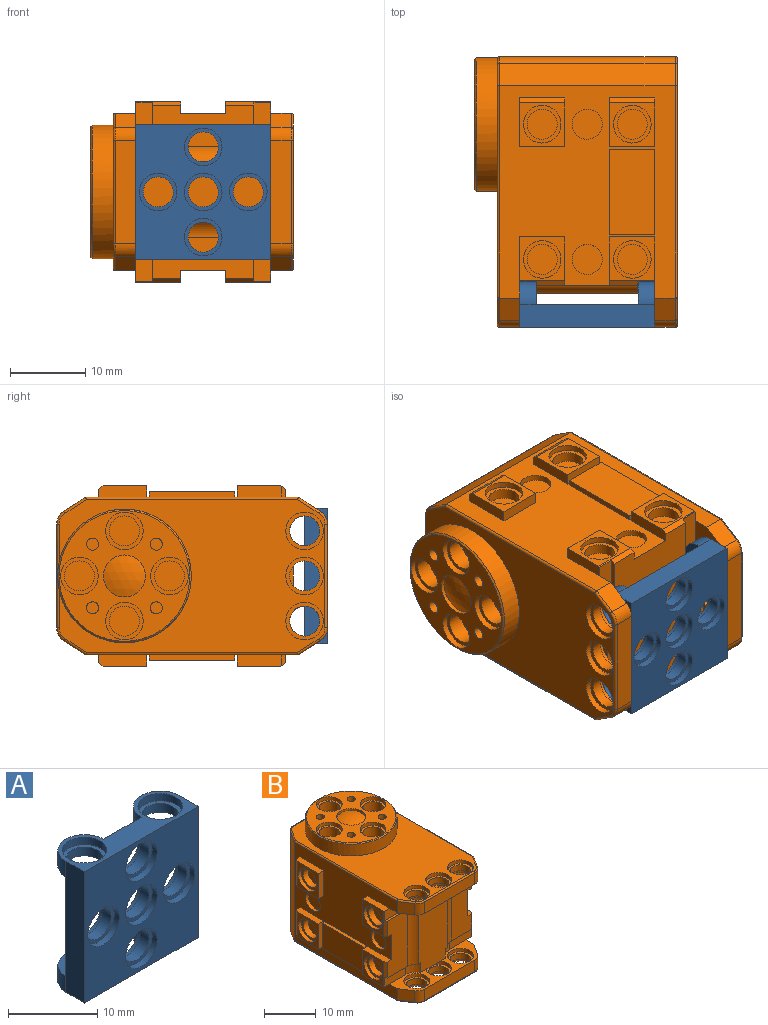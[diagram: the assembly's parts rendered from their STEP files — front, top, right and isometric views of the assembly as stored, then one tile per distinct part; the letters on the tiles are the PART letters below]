
ASSEMBLY  parts=2 mates=1
PART A: 59 faces, bbox 18x6x18 mm
  f0: plane 18x6mm, normal (0,0,-1), area 43mm2, adj f50,f51,f52,f53,f54,f55,f56,f58
  f1: plane 5x5mm, normal (0,0,1), area 7.1mm2, adj f13,f15
  f2: plane 5x5mm, normal (0,0,1), area 7.1mm2, adj f14,f16
  f3: cylinder r=2mm len=4mm, axis (0,1,0), area 17.6mm2, adj f8,f17
  f4: cylinder r=2mm len=4mm, axis (0,1,0), area 17.6mm2, adj f9,f18
  f5: cylinder r=2mm len=4mm, axis (0,1,0), area 17.6mm2, adj f10,f19
  f6: cylinder r=2mm len=4mm, axis (0,1,0), area 17.6mm2, adj f11,f20
  f7: cylinder r=2mm len=4mm, axis (0,1,0), area 17.6mm2, adj f12,f21
  f8: plane 5x5mm, normal (0,-1,0), area 7.1mm2, adj f3,f23
  f9: plane 5x5mm, normal (0,-1,0), area 7.1mm2, adj f4,f24
  f10: plane 5x5mm, normal (0,-1,0), area 7.1mm2, adj f5,f25
  f11: plane 5x5mm, normal (0,-1,0), area 7.1mm2, adj f6,f26
  f12: plane 5x5mm, normal (0,-1,0), area 7.1mm2, adj f7,f27
  f13: cylinder r=2mm len=4mm, axis (0,0,-1), area 15.1mm2, adj f1,f31
  f14: cylinder r=2mm len=4mm, axis (0,0,-1), area 15.1mm2, adj f2,f40
  f15: cylinder r=2.5mm len=5mm, axis (0,0,-1), area 15.7mm2, adj f1,f42
  f16: cylinder r=2.5mm len=5mm, axis (0,0,-1), area 15.7mm2, adj f2,f42
  f17: plane 5x5mm, normal (0,1,0), area 7.1mm2, adj f3,f43
  f18: plane 5x5mm, normal (0,1,0), area 7.1mm2, adj f4,f44
  f19: plane 5x5mm, normal (0,1,0), area 7.1mm2, adj f5,f45
  f20: plane 5x5mm, normal (0,1,0), area 7.1mm2, adj f6,f46
  f21: plane 5x5mm, normal (0,1,0), area 7.1mm2, adj f7,f47
  f22: cylinder r=2mm len=4mm, axis (0,0,1), area 15.1mm2, adj f34,f48
  f23: cylinder r=2.5mm len=5mm, axis (0,1,0), area 12.6mm2, adj f8,f52
  f24: cylinder r=2.5mm len=5mm, axis (0,1,0), area 12.6mm2, adj f9,f52
  f25: cylinder r=2.5mm len=5mm, axis (0,1,0), area 12.6mm2, adj f10,f52
  f26: cylinder r=2.5mm len=5mm, axis (0,1,0), area 12.6mm2, adj f11,f52
  f27: cylinder r=2.5mm len=5mm, axis (0,1,0), area 12.6mm2, adj f12,f52
  f28: cylinder r=3mm len=6mm, axis (0,0,-1), area 20.7mm2, adj f31,f42,f51,f55
  f29: plane 5x2.5mm, normal (0,0,1), area 9.8mm2, adj f30,f55
  f30: cylinder r=2.5mm len=5mm, axis (0,0,-1), area 6.3mm2, adj f29,f31,f55
  f31: plane 6x5.5mm, normal (0,0,-1), area 11.4mm2, adj f13,f28,f30,f55
  f32: plane 5x2.5mm, normal (0,0,-1), area 9.8mm2, adj f33,f55
  f33: cylinder r=2.5mm len=5mm, axis (0,0,1), area 6.3mm2, adj f32,f34,f55
  f34: plane 6x5.5mm, normal (0,0,1), area 11.4mm2, adj f22,f33,f50,f55
  f35: plane 5x2.5mm, normal (0,0,-1), area 9.8mm2, adj f36,f55
  f36: cylinder r=2.5mm len=5mm, axis (0,0,1), area 6.3mm2, adj f35,f37,f55
  f37: plane 6x5.5mm, normal (0,0,1), area 11.4mm2, adj f36,f49,f54,f55
  f38: plane 5x2.5mm, normal (0,0,1), area 9.8mm2, adj f39,f55
  f39: cylinder r=2.5mm len=5mm, axis (0,0,-1), area 6.3mm2, adj f38,f40,f55
  f40: plane 6x5.5mm, normal (0,0,-1), area 11.4mm2, adj f14,f39,f41,f55
  f41: cylinder r=3mm len=6mm, axis (0,0,-1), area 20.7mm2, adj f40,f42,f53,f55
  f42: plane 18x6mm, normal (0,0,1), area 43mm2, adj f15,f16,f28,f41,f51,f52,f53,f55
  f43: cylinder r=2.5mm len=5mm, axis (0,-1,0), area 12.6mm2, adj f17,f55
  f44: cylinder r=2.5mm len=5mm, axis (0,-1,0), area 12.6mm2, adj f18,f55
  f45: cylinder r=2.5mm len=5mm, axis (0,-1,0), area 12.6mm2, adj f19,f55
  f46: cylinder r=2.5mm len=5mm, axis (0,-1,0), area 12.6mm2, adj f20,f55
  f47: cylinder r=2.5mm len=5mm, axis (0,-1,0), area 12.6mm2, adj f21,f55
  f48: plane 5x5mm, normal (0,0,-1), area 7.1mm2, adj f22,f56
  f49: cylinder r=2mm len=4mm, axis (0,0,1), area 15.1mm2, adj f37,f57
  f50: cylinder r=3mm len=6mm, axis (0,0,1), area 20.7mm2, adj f0,f34,f51,f55
  f51: plane 18x3mm, normal (-1,0,0), area 54mm2, adj f0,f28,f42,f50,f52,f55
  f52: plane 18x18mm, normal (0,-1,0), area 225.8mm2, adj f0,f23,f24,f25,f26,f27,f42,f51
  f53: plane 18x3mm, normal (1,0,0), area 54mm2, adj f0,f41,f42,f52,f54,f55
  f54: cylinder r=3mm len=6mm, axis (0,0,1), area 20.7mm2, adj f0,f37,f53,f55
  f55: plane 18x18mm, normal (0,1,0), area 157mm2, adj f0,f28,f29,f30,f31,f32,f33,f34
  f56: cylinder r=2.5mm len=5mm, axis (0,0,1), area 15.7mm2, adj f0,f48
  f57: plane 5x5mm, normal (0,0,-1), area 7.1mm2, adj f49,f58
  f58: cylinder r=2.5mm len=5mm, axis (0,0,1), area 15.7mm2, adj f0,f57
PART B: 229 faces, bbox 24x36.3x27 mm
  f0: torus R=1.7mm, axis (0,0,1), area 0.9mm2, adj f2,f5,f98,f144
  f1: torus R=1.7mm, axis (0,0,1), area 0.9mm2, adj f4,f6,f98,f144
  f2: cylinder r=0.3mm len=3.1mm, axis (-0.54,0.84,0), area 1.6mm2, adj f0,f11,f144,f150
  f3: cylinder r=2.5mm len=13.5mm, axis (0,0,-1), area 31.3mm2, adj f103,f104,f129,f154
  f4: cylinder r=0.3mm len=3.1mm, axis (-0.54,-0.84,0), area 1.6mm2, adj f1,f14,f144,f170
  f5: cylinder r=2mm len=2.7mm, axis (0,0,-1), area 5.4mm2, adj f0,f132,f150,f179
  f6: cylinder r=2mm len=2.7mm, axis (0,0,-1), area 5.4mm2, adj f1,f132,f170,f179
  f7: cylinder r=0.3mm len=3.1mm, axis (0.54,-0.84,0), area 1.6mm2, adj f8,f14,f144,f207
  f8: torus R=1.7mm, axis (0,0,-1), area 0.9mm2, adj f7,f144,f191,f208
  f9: cylinder r=8.9mm len=17.8mm, axis (0,0,-1), area 156.6mm2, adj f97,f144,f191
  f10: cylinder r=2.5mm len=5mm, axis (0,0,-1), area 12.6mm2, adj f171,f199
  f11: cylinder r=0.3mm len=28.3mm, axis (0,1,0), area 13.3mm2, adj f2,f144,f193,f200
  f12: cylinder r=2mm len=4mm, axis (-1,0,0), area 10.1mm2, adj f109,f200
  f13: cylinder r=2mm len=4mm, axis (-1,0,0), area 10.1mm2, adj f110,f200
  f14: cylinder r=0.3mm len=28.3mm, axis (0,-1,0), area 13.3mm2, adj f4,f7,f144,f206
  f15: cylinder r=2mm len=4mm, axis (-1,0,0), area 10.1mm2, adj f138,f206
  f16: cylinder r=2mm len=4mm, axis (-1,0,0), area 10.1mm2, adj f139,f206
  f17: plane 11.4x0.7mm, normal (0,0,-1), area 8mm2, adj f137,f180,f182,f206
  f18: cylinder r=2.5mm len=5mm, axis (0,0,1), area 12.6mm2, adj f19,f20
  f19: plane 35.4x20.4mm, normal (0,0,-1), area 586.6mm2, adj f18,f21,f22,f23,f24,f25,f26,f218
  f20: plane 5x5mm, normal (0,0,-1), area 7.1mm2, adj f18,f217
  f21: cylinder r=2.5mm len=5mm, axis (0,0,1), area 12.6mm2, adj f19,f216
  f22: torus R=1.7mm, axis (0,0,1), area 0.9mm2, adj f19,f202,f219,f220
  f23: torus R=1.7mm, axis (0,0,1), area 0.9mm2, adj f19,f204,f220,f221
  f24: cylinder r=0.3mm len=3.1mm, axis (-0.54,0.84,0), area 1.6mm2, adj f19,f25,f207,f222
  f25: torus R=1.7mm, axis (0,0,-1), area 0.9mm2, adj f19,f24,f208,f223
  f26: torus R=1.7mm, axis (0,0,-1), area 0.9mm2, adj f19,f210,f223,f224
  f27: plane 4x4mm, normal (0,0,1), area 12.6mm2, adj f31
  f28: plane 4x4mm, normal (0,0,1), area 12.6mm2, adj f32
  f29: plane 4x4mm, normal (0,0,1), area 12.6mm2, adj f33
  f30: plane 4x4mm, normal (0,0,1), area 12.6mm2, adj f34
  f31: cylinder r=2mm len=4mm, axis (0,0,-1), area 27.6mm2, adj f27,f48
  f32: cylinder r=2mm len=4mm, axis (0,0,-1), area 27.6mm2, adj f28,f49
  f33: cylinder r=2mm len=4mm, axis (0,0,-1), area 27.6mm2, adj f29,f50
  f34: cylinder r=2mm len=4mm, axis (0,0,-1), area 27.6mm2, adj f30,f51
  f35: plane 4x4mm, normal (-1,0,0), area 12.6mm2, adj f52
  f36: plane 4x4mm, normal (-1,0,0), area 12.6mm2, adj f53
  f37: plane 4x4mm, normal (-1,0,0), area 12.6mm2, adj f54
  f38: plane 4x4mm, normal (-1,0,0), area 12.6mm2, adj f55
  f39: plane 4x4mm, normal (1,0,0), area 12.6mm2, adj f56
  f40: plane 4x4mm, normal (1,0,0), area 12.6mm2, adj f57
  f41: plane 4x4mm, normal (1,0,0), area 12.6mm2, adj f58
  f42: plane 4x4mm, normal (1,0,0), area 12.6mm2, adj f59
  f43: plane 1.6x1.6mm, normal (0,0,1), area 2mm2, adj f60
  f44: plane 1.6x1.6mm, normal (0,0,1), area 2mm2, adj f61
  f45: plane 1.6x1.6mm, normal (0,0,1), area 2mm2, adj f62
  f46: plane 1.6x1.6mm, normal (0,0,1), area 2mm2, adj f63
  f47: sphere r=8.09mm, area 25.4mm2, adj f64
  f48: plane 5x5mm, normal (0,0,1), area 7.1mm2, adj f31,f65
  f49: plane 5x5mm, normal (0,0,1), area 7.1mm2, adj f32,f66
  f50: plane 5x5mm, normal (0,0,1), area 7.1mm2, adj f33,f67
  f51: plane 5x5mm, normal (0,0,1), area 7.1mm2, adj f34,f68
  f52: cylinder r=2mm len=4mm, axis (-1,0,0), area 17.6mm2, adj f35,f69
  f53: cylinder r=2mm len=4mm, axis (-1,0,0), area 17.6mm2, adj f36,f70
  f54: cylinder r=2mm len=4mm, axis (-1,0,0), area 17.6mm2, adj f37,f71
  f55: cylinder r=2mm len=4mm, axis (-1,0,0), area 17.6mm2, adj f38,f72
  f56: cylinder r=2mm len=4mm, axis (-1,0,0), area 17.6mm2, adj f39,f73
  f57: cylinder r=2mm len=4mm, axis (-1,0,0), area 17.6mm2, adj f40,f74
  f58: cylinder r=2mm len=4mm, axis (-1,0,0), area 17.6mm2, adj f41,f78
  f59: cylinder r=2mm len=4mm, axis (-1,0,0), area 17.6mm2, adj f42,f79
  f60: cylinder r=0.8mm len=3mm, axis (0,0,-1), area 15.1mm2, adj f43,f80
  f61: cylinder r=0.8mm len=3mm, axis (0,0,-1), area 15.1mm2, adj f44,f80
  f62: cylinder r=0.8mm len=3mm, axis (0,0,-1), area 15.1mm2, adj f45,f80
  f63: cylinder r=0.8mm len=3mm, axis (0,0,-1), area 15.1mm2, adj f46,f80
  f64: cylinder r=2.8mm len=5.6mm, axis (0,0,-1), area 8.8mm2, adj f47,f80
  f65: cylinder r=2.5mm len=5mm, axis (0,0,-1), area 12.6mm2, adj f48,f80
  f66: cylinder r=2.5mm len=5mm, axis (0,0,-1), area 12.6mm2, adj f49,f80
  f67: cylinder r=2.5mm len=5mm, axis (0,0,-1), area 12.6mm2, adj f50,f80
  f68: cylinder r=2.5mm len=5mm, axis (0,0,-1), area 12.6mm2, adj f51,f80
  f69: plane 5x5mm, normal (-1,0,0), area 7.1mm2, adj f52,f84
  f70: plane 5x5mm, normal (-1,0,0), area 7.1mm2, adj f53,f85
  f71: plane 5x5mm, normal (-1,0,0), area 7.1mm2, adj f54,f86
  f72: plane 5x5mm, normal (-1,0,0), area 7.1mm2, adj f55,f87
  f73: plane 5x5mm, normal (1,0,0), area 7.1mm2, adj f56,f88
  f74: plane 5x5mm, normal (1,0,0), area 7.1mm2, adj f57,f89
  f75: cylinder r=2mm len=4mm, axis (0,0,-1), area 17.6mm2, adj f82,f90
  f76: cylinder r=2mm len=4mm, axis (0,0,-1), area 17.6mm2, adj f81,f93
  f77: cylinder r=2mm len=4mm, axis (0,0,-1), area 17.6mm2, adj f83,f94
  f78: plane 5x5mm, normal (1,0,0), area 7.1mm2, adj f58,f95
  f79: plane 5x5mm, normal (1,0,0), area 7.1mm2, adj f59,f96
  f80: plane 17.4x17.4mm, normal (0,0,1), area 126.6mm2, adj f60,f61,f62,f63,f64,f65,f66,f67
  f81: plane 5x5mm, normal (0,0,1), area 7.1mm2, adj f76,f99
  f82: plane 5x5mm, normal (0,0,1), area 7.1mm2, adj f75,f100
  f83: plane 5x5mm, normal (0,0,1), area 7.1mm2, adj f77,f101
  f84: cylinder r=2.5mm len=5mm, axis (-1,0,0), area 12.6mm2, adj f69,f102
  f85: cylinder r=2.5mm len=5mm, axis (-1,0,0), area 12.6mm2, adj f70,f107
  f86: cylinder r=2.5mm len=5mm, axis (-1,0,0), area 12.6mm2, adj f71,f112
  f87: cylinder r=2.5mm len=5mm, axis (-1,0,0), area 12.6mm2, adj f72,f114
  f88: cylinder r=2.5mm len=5mm, axis (-1,0,0), area 12.6mm2, adj f73,f121
  f89: cylinder r=2.5mm len=5mm, axis (-1,0,0), area 12.6mm2, adj f74,f127
  f90: plane 5x5mm, normal (0,0,-1), area 7.1mm2, adj f75,f128
  f91: plane 4x1mm, normal (0,0,-1), area 2.8mm2, adj f115,f129
  f92: plane 4x1mm, normal (0,0,1), area 2.8mm2, adj f128,f129
  f93: plane 5x5mm, normal (0,0,-1), area 7.1mm2, adj f76,f135
  f94: plane 5x5mm, normal (0,0,-1), area 7.1mm2, adj f77,f136
  f95: cylinder r=2.5mm len=5mm, axis (-1,0,0), area 12.6mm2, adj f78,f141
  f96: cylinder r=2.5mm len=5mm, axis (-1,0,0), area 12.6mm2, adj f79,f143
  f97: cone r=707.11mm half-angle=45deg, axis (0,0,-1), area 15.6mm2, adj f9,f80
  f98: cylinder r=0.3mm len=13.83mm, axis (-1,0,0), area 6.5mm2, adj f0,f1,f132,f144
  f99: cylinder r=2.5mm len=5mm, axis (0,0,-1), area 12.6mm2, adj f81,f144
  f100: cylinder r=2.5mm len=5mm, axis (0,0,-1), area 12.6mm2, adj f82,f144
  f101: cylinder r=2.5mm len=5mm, axis (0,0,-1), area 12.6mm2, adj f83,f144
  f102: plane 6x5.84mm, normal (-1,0,0), area 15.4mm2, adj f84,f105,f151,f152,f153
  f103: plane 8.54x1.53mm, normal (0,0,-1), area 4.5mm2, adj f3,f106,f116,f117,f129,f154
  f104: plane 8.54x1.53mm, normal (0,0,1), area 4.5mm2, adj f3,f105,f129,f130,f131,f154
  f105: plane 6x0.66mm, normal (-0.84,-0.54,0), area 3.3mm2, adj f102,f104,f131,f151,f153,f154
  f106: plane 6x0.66mm, normal (-0.84,-0.54,0), area 3.3mm2, adj f103,f107,f117,f154,f155,f157
  f107: plane 6x5.84mm, normal (-1,0,0), area 15.4mm2, adj f85,f106,f155,f156,f157
  f108: plane 11.4x6mm, normal (-1,0,0), area 68.4mm2, adj f158,f159,f160,f161
  f109: plane 4x4mm, normal (-1,0,0), area 12.6mm2, adj f12
  f110: plane 4x4mm, normal (-1,0,0), area 12.6mm2, adj f13
  f111: plane 6x0.66mm, normal (-0.84,0.54,0), area 4.7mm2, adj f112,f163,f164,f165
  f112: plane 6x5.84mm, normal (-1,0,0), area 15.4mm2, adj f86,f111,f162,f163,f165
  f113: plane 6x0.66mm, normal (-0.84,0.54,0), area 4.7mm2, adj f114,f167,f168,f169
  f114: plane 6x5.84mm, normal (-1,0,0), area 15.4mm2, adj f87,f113,f166,f167,f169
  f115: cylinder r=2.5mm len=5mm, axis (0,0,-1), area 12.6mm2, adj f91,f145,f171
  f116: cylinder r=3.02mm len=2.63mm, axis (0,0,-1), area 7.2mm2, adj f103,f117,f129,f171
  f117: plane 5.91x2.25mm, normal (0,-1,0), area 13.3mm2, adj f103,f106,f116,f157,f171
  f118: cylinder r=3.02mm len=2.63mm, axis (0,0,-1), area 7.2mm2, adj f120,f124,f129,f171
  f119: cylinder r=2.5mm len=5mm, axis (0,0,-1), area 12.6mm2, adj f146,f171
  f120: plane 5.91x2.25mm, normal (0,-1,0), area 13.3mm2, adj f118,f124,f125,f171,f172
  f121: plane 6x5.84mm, normal (1,0,0), area 15.4mm2, adj f88,f125,f172,f173,f174
  f122: plane 8.54x1.53mm, normal (0,0,1), area 4.5mm2, adj f123,f126,f129,f133,f134,f175
  f123: cylinder r=2.5mm len=13.5mm, axis (0,0,-1), area 31.3mm2, adj f122,f124,f129,f175
  f124: plane 8.54x1.53mm, normal (0,0,-1), area 4.5mm2, adj f118,f120,f123,f125,f129,f175
  f125: plane 6x0.66mm, normal (0.84,-0.54,0), area 3.3mm2, adj f120,f121,f124,f172,f174,f175
  f126: plane 6x0.66mm, normal (0.84,-0.54,0), area 3.3mm2, adj f122,f127,f133,f175,f176,f178
  f127: plane 6x5.84mm, normal (1,0,0), area 15.4mm2, adj f89,f126,f176,f177,f178
  f128: cylinder r=2.5mm len=5mm, axis (0,0,-1), area 12.6mm2, adj f90,f92,f179
  f129: plane 18x8mm, normal (0,-1,0), area 138.4mm2, adj f3,f91,f92,f103,f104,f116,f118,f122
  f130: cylinder r=3.02mm len=2.63mm, axis (0,0,-1), area 7.2mm2, adj f104,f129,f131,f179
  f131: plane 5.91x2.25mm, normal (0,-1,0), area 13.3mm2, adj f104,f105,f130,f151,f179
  f132: plane 13.83x2.7mm, normal (0,-1,0), area 37.3mm2, adj f5,f6,f98,f179
  f133: plane 5.91x2.25mm, normal (0,-1,0), area 13.3mm2, adj f122,f126,f134,f178,f179
  f134: cylinder r=3.02mm len=2.63mm, axis (0,0,-1), area 7.2mm2, adj f122,f129,f133,f179
  f135: cylinder r=2.5mm len=5mm, axis (0,0,-1), area 12.6mm2, adj f93,f179
  f136: cylinder r=2.5mm len=5mm, axis (0,0,-1), area 12.6mm2, adj f94,f179
  f137: plane 11.4x6mm, normal (1,0,0), area 68.4mm2, adj f17,f180,f181,f182
  f138: plane 4x4mm, normal (1,0,0), area 12.6mm2, adj f15
  f139: plane 4x4mm, normal (1,0,0), area 12.6mm2, adj f16
  f140: plane 6x0.66mm, normal (0.84,0.54,0), area 4.7mm2, adj f141,f184,f185,f186
  f141: plane 6x5.84mm, normal (1,0,0), area 15.4mm2, adj f95,f140,f183,f184,f186
  f142: plane 6x0.66mm, normal (0.84,0.54,0), area 4.7mm2, adj f143,f188,f189,f190
  f143: plane 6x5.84mm, normal (1,0,0), area 15.4mm2, adj f96,f142,f187,f188,f190
  f144: plane 35.4x20.4mm, normal (0,0,1), area 397.2mm2, adj f0,f1,f2,f4,f7,f8,f9,f11
  f145: plane 5x5mm, normal (0,0,1), area 7.1mm2, adj f115,f194
  f146: plane 5x5mm, normal (0,0,1), area 7.1mm2, adj f119,f195
  f147: plane 4x4mm, normal (0,0,-1), area 12.6mm2, adj f196
  f148: plane 4x4mm, normal (0,0,-1), area 12.6mm2, adj f197
  f149: plane 4x4mm, normal (0,0,-1), area 12.6mm2, adj f198
  f150: plane 2.94x2.7mm, normal (-0.84,-0.54,0), area 9.5mm2, adj f2,f5,f179,f200
  f151: plane 5.98x1.5mm, normal (0,0,1), area 9mm2, adj f102,f105,f131,f152,f200
  f152: plane 6x1.5mm, normal (0,1,0), area 9mm2, adj f102,f151,f153,f200
  f153: plane 6.5x1.5mm, normal (0,0,-1), area 9.6mm2, adj f102,f105,f152,f154,f200
  f154: plane 13.5x5.57mm, normal (0,-1,0), area 68.8mm2, adj f3,f103,f104,f105,f106,f153,f155,f200
  f155: plane 6.5x1.5mm, normal (0,0,1), area 9.6mm2, adj f106,f107,f154,f156,f200
  f156: plane 6x1.5mm, normal (0,1,0), area 9mm2, adj f107,f155,f157,f200
  f157: plane 5.98x1.5mm, normal (0,0,-1), area 9mm2, adj f106,f107,f117,f156,f200
  f158: plane 6x0.7mm, normal (0,-1,0), area 4.2mm2, adj f108,f159,f161,f200
  f159: plane 11.4x0.7mm, normal (0,0,1), area 8mm2, adj f108,f158,f160,f200
  f160: plane 6x0.7mm, normal (0,1,0), area 4.2mm2, adj f108,f159,f161,f200
  f161: plane 11.4x0.7mm, normal (0,0,-1), area 8mm2, adj f108,f158,f160,f200
  f162: plane 6x1.5mm, normal (0,-1,0), area 9mm2, adj f112,f163,f165,f200
  f163: plane 6.5x1.5mm, normal (0,0,1), area 9.6mm2, adj f111,f112,f162,f164,f200
  f164: plane 6x1.07mm, normal (0,1,0), area 6.4mm2, adj f111,f163,f165,f200
  f165: plane 6.5x1.5mm, normal (0,0,-1), area 9.6mm2, adj f111,f112,f162,f164,f200
  f166: plane 6x1.5mm, normal (0,-1,0), area 9mm2, adj f114,f167,f169,f200
  f167: plane 6.5x1.5mm, normal (0,0,1), area 9.6mm2, adj f113,f114,f166,f168,f200
  f168: plane 6x1.07mm, normal (0,1,0), area 6.4mm2, adj f113,f167,f169,f200
  f169: plane 6.5x1.5mm, normal (0,0,-1), area 9.6mm2, adj f113,f114,f166,f168,f200
  f170: plane 2.94x2.7mm, normal (0.84,-0.54,0), area 9.5mm2, adj f4,f6,f179,f206
  f171: plane 21x6.03mm, normal (0,0,1), area 47.8mm2, adj f10,f115,f116,f117,f118,f119,f120,f129
  f172: plane 5.98x1.5mm, normal (0,0,-1), area 9mm2, adj f120,f121,f125,f173,f206
  f173: plane 6x1.5mm, normal (0,1,0), area 9mm2, adj f121,f172,f174,f206
  f174: plane 6.5x1.5mm, normal (0,0,1), area 9.6mm2, adj f121,f125,f173,f175,f206
  f175: plane 13.5x5.57mm, normal (0,-1,0), area 68.8mm2, adj f122,f123,f124,f125,f126,f174,f176,f206
  f176: plane 6.5x1.5mm, normal (0,0,-1), area 9.6mm2, adj f126,f127,f175,f177,f206
  f177: plane 6x1.5mm, normal (0,1,0), area 9mm2, adj f127,f176,f178,f206
  f178: plane 5.98x1.5mm, normal (0,0,1), area 9mm2, adj f126,f127,f133,f177,f206
  f179: plane 21x6.03mm, normal (0,0,-1), area 47.8mm2, adj f5,f6,f128,f129,f130,f131,f132,f133
  f180: plane 6x0.7mm, normal (0,1,0), area 4.2mm2, adj f17,f137,f181,f206
  f181: plane 11.4x0.7mm, normal (0,0,1), area 8mm2, adj f137,f180,f182,f206
  f182: plane 6x0.7mm, normal (0,-1,0), area 4.2mm2, adj f17,f137,f181,f206
  f183: plane 6x1.5mm, normal (0,-1,0), area 9mm2, adj f141,f184,f186,f206
  f184: plane 6.5x1.5mm, normal (0,0,-1), area 9.6mm2, adj f140,f141,f183,f185,f206
  f185: plane 6x1.07mm, normal (0,1,0), area 6.4mm2, adj f140,f184,f186,f206
  f186: plane 6.5x1.5mm, normal (0,0,1), area 9.6mm2, adj f140,f141,f183,f185,f206
  f187: plane 6x1.5mm, normal (0,-1,0), area 9mm2, adj f143,f188,f190,f206
  f188: plane 6.5x1.5mm, normal (0,0,-1), area 9.6mm2, adj f142,f143,f187,f189,f206
  f189: plane 6x1.07mm, normal (0,1,0), area 6.4mm2, adj f142,f188,f190,f206
  f190: plane 6.5x1.5mm, normal (0,0,1), area 9.6mm2, adj f142,f143,f187,f189,f206
  f191: cylinder r=0.3mm len=13.83mm, axis (1,0,0), area 6mm2, adj f8,f9,f144,f192,f209
  f192: torus R=1.7mm, axis (0,0,-1), area 0.9mm2, adj f144,f191,f193,f210
  f193: cylinder r=0.3mm len=3.1mm, axis (0.54,0.84,0), area 1.6mm2, adj f11,f144,f192,f211
  f194: cylinder r=2mm len=4mm, axis (0,0,-1), area 17.6mm2, adj f145,f212
  f195: cylinder r=2mm len=4mm, axis (0,0,-1), area 17.6mm2, adj f146,f213
  f196: cylinder r=2mm len=4mm, axis (0,0,1), area 27.6mm2, adj f147,f214
  f197: cylinder r=2mm len=4mm, axis (0,0,1), area 27.6mm2, adj f148,f215
  f198: cylinder r=2mm len=4mm, axis (0,0,1), area 27.6mm2, adj f149,f216
  f199: plane 5x5mm, normal (0,0,1), area 7.1mm2, adj f10,f217
  f200: plane 28.3x23.4mm, normal (-1,0,0), area 383mm2, adj f11,f12,f13,f150,f151,f152,f153,f154
  f201: plane 2.94x2.7mm, normal (-0.84,-0.54,0), area 9.5mm2, adj f171,f200,f202,f219
  f202: cylinder r=2mm len=2.7mm, axis (0,0,-1), area 5.4mm2, adj f22,f171,f201,f203
  f203: plane 13.83x2.7mm, normal (0,-1,0), area 37.3mm2, adj f171,f202,f204,f220
  f204: cylinder r=2mm len=2.7mm, axis (0,0,-1), area 5.4mm2, adj f23,f171,f203,f205
  f205: plane 2.94x2.7mm, normal (0.84,-0.54,0), area 9.5mm2, adj f171,f204,f206,f221
  f206: plane 28.3x23.4mm, normal (1,0,0), area 383mm2, adj f14,f15,f16,f17,f170,f171,f172,f173
  f207: plane 23.4x2.94mm, normal (0.84,0.54,0), area 82mm2, adj f7,f24,f206,f208
  f208: cylinder r=2mm len=23.4mm, axis (0,0,1), area 46.6mm2, adj f8,f25,f207,f209
  f209: plane 23.4x13.83mm, normal (0,1,0), area 323.6mm2, adj f191,f208,f210,f223
  f210: cylinder r=2mm len=23.4mm, axis (0,0,1), area 46.6mm2, adj f26,f192,f209,f211
  f211: plane 23.4x2.94mm, normal (-0.84,0.54,0), area 82mm2, adj f193,f200,f210,f224
  f212: plane 5x5mm, normal (0,0,-1), area 7.1mm2, adj f194,f225
  f213: plane 5x5mm, normal (0,0,-1), area 7.1mm2, adj f195,f226
  f214: plane 5x5mm, normal (0,0,-1), area 7.1mm2, adj f196,f227
  f215: plane 5x5mm, normal (0,0,-1), area 7.1mm2, adj f197,f228
  f216: plane 5x5mm, normal (0,0,-1), area 7.1mm2, adj f21,f198
  f217: cylinder r=2mm len=4mm, axis (0,0,-1), area 17.6mm2, adj f20,f199
  f218: cylinder r=0.3mm len=28.3mm, axis (0,-1,0), area 13.3mm2, adj f19,f200,f219,f224
  f219: cylinder r=0.3mm len=3.1mm, axis (0.54,-0.84,0), area 1.6mm2, adj f19,f22,f201,f218
  f220: cylinder r=0.3mm len=13.83mm, axis (1,0,0), area 6.5mm2, adj f19,f22,f23,f203
  f221: cylinder r=0.3mm len=3.1mm, axis (0.54,0.84,0), area 1.6mm2, adj f19,f23,f205,f222
  f222: cylinder r=0.3mm len=28.3mm, axis (0,1,0), area 13.3mm2, adj f19,f24,f206,f221
  f223: cylinder r=0.3mm len=13.83mm, axis (-1,0,0), area 6.5mm2, adj f19,f25,f26,f209
  f224: cylinder r=0.3mm len=3.1mm, axis (-0.54,-0.84,0), area 1.6mm2, adj f19,f26,f211,f218
  f225: cylinder r=2.5mm len=5mm, axis (0,0,1), area 12.6mm2, adj f19,f212
  f226: cylinder r=2.5mm len=5mm, axis (0,0,1), area 12.6mm2, adj f19,f213
  f227: cylinder r=2.5mm len=5mm, axis (0,0,1), area 12.6mm2, adj f19,f214
  f228: cylinder r=2.5mm len=5mm, axis (0,0,1), area 12.6mm2, adj f19,f215
PLACE A rot(axis=(0,-1,0),90deg) t=(-36,-12.4,21.6)mm
PLACE B rot(axis=(0,-1,0),90deg) t=(-36,11.6,21.6)mm
MATE fastened A.f13 <-> B.f3  axis (-1,0,0) through (-45,-12.4,15.6)mm
